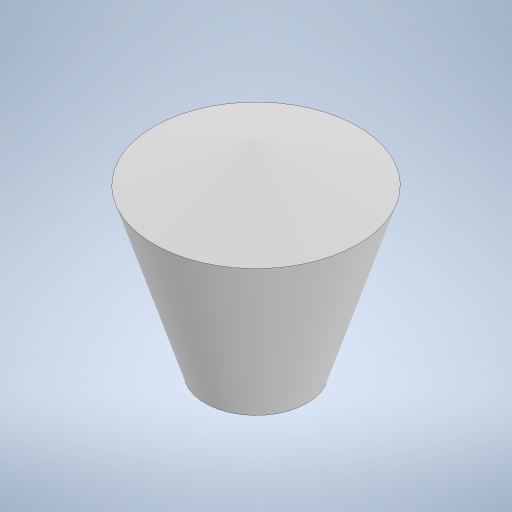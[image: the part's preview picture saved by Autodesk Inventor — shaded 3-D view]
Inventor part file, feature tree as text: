
AUTODESK INVENTOR PART (.ipt)
format: ipt  version: 2024 (Build 280153000, 153)  size: 232,448 bytes
history: native  units: mm
features: revolve x1, sketch x1
ambient origin geometry x8: Origin, YZ Plane, XZ Plane, XY Plane, X Axis, Y Axis, Z Axis, Center Point
bodies: Solid1 (feature_tree)
feature tree (2):
  revolve  "Revolution1"  [1 undecoded]
  sketch  "Sketch1"  dims[d0=8.0mm d1=1.0mm d2=20.0mm d3=4.0mm d6=10.0mm d8=4.0mm d9=90.0deg]
note: 1 required parameter value undecoded (feature->parameter linkage not recoverable at this tier; creation-order binding heuristic only, values carry confidence <= 0.55)
